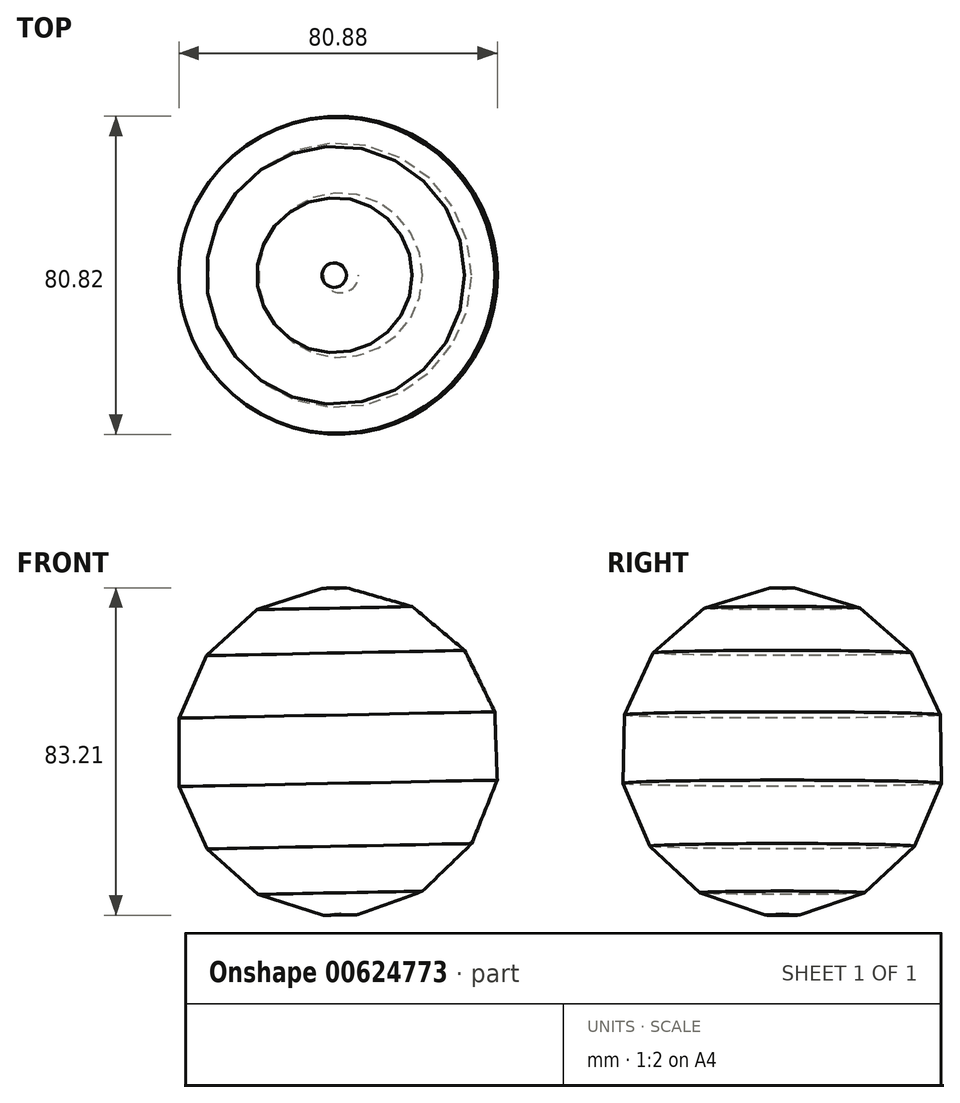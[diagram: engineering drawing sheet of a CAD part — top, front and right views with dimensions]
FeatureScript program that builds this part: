
annotation { "Feature Type Name" : "Feature", "Feature Type Description" : "" }
export const myFeature = defineFeature(function(context is Context, id is Id, definition is map)
    precondition{}
    {
        {
            var Q0;
            Q0=qCreatedBy(makeId("Front.planeOp"),FACE);
            var sketch = newSketch(context, id + "F0", { "sketchPlane" : qUnion([Q0])});
            skCircle(sketch, "E0.cCircle", {"center": v(-26.3, 29.34) * mm, "radius": 40.86 * mm, "construction": true});
            skLineSegment(sketch, "E0.0", {"start": v(8.37, 6.04) * mm, "end": v(-4.1, -6.04) * mm});
            skLineSegment(sketch, "E0.1", {"start": v(-4.1, -6.04) * mm, "end": v(-20.42, -12.01) * mm});
            skLineSegment(sketch, "E0.2", {"start": v(-20.42, -12.01) * mm, "end": v(-37.75, -10.83) * mm});
            skLineSegment(sketch, "E0.3", {"start": v(-37.75, -10.83) * mm, "end": v(-53.1, -2.7) * mm});
            skLineSegment(sketch, "E0.4", {"start": v(-53.1, -2.7) * mm, "end": v(-63.81, 10.97) * mm});
            skLineSegment(sketch, "E0.5", {"start": v(-63.81, 10.97) * mm, "end": v(-68.04, 27.82) * mm});
            skLineSegment(sketch, "E0.6", {"start": v(-68.04, 27.82) * mm, "end": v(-65.05, 44.93) * mm});
            skLineSegment(sketch, "E0.7", {"start": v(-65.05, 44.93) * mm, "end": v(-55.36, 59.34) * mm});
            skLineSegment(sketch, "E0.8", {"start": v(-55.36, 59.34) * mm, "end": v(-40.65, 68.57) * mm});
            skLineSegment(sketch, "E0.9", {"start": v(-40.65, 68.57) * mm, "end": v(-23.45, 71.02) * mm});
            skLineSegment(sketch, "E0.10", {"start": v(-23.45, 71.02) * mm, "end": v(-6.75, 66.26) * mm});
            skLineSegment(sketch, "E0.11", {"start": v(-6.75, 66.26) * mm, "end": v(6.58, 55.11) * mm});
            skLineSegment(sketch, "E0.12", {"start": v(6.58, 55.11) * mm, "end": v(14.22, 39.52) * mm});
            skLineSegment(sketch, "E0.13", {"start": v(14.22, 39.52) * mm, "end": v(14.85, 22.16) * mm});
            skLineSegment(sketch, "E0.14", {"start": v(14.85, 22.16) * mm, "end": v(8.37, 6.04) * mm});
            skPoint(sketch, "E0.0.midPoint", {"position": v(2.13, 0) * mm});
            skLineSegment(sketch, "E1", {"start": v(-26.7, 78.08) * mm, "end": v(-24.47, -32.39) * mm});
            skSolve(sketch);
        }
        {
            var Q0;
            Q0=makeQuery(id+"F0.imprint","IMPRINT",FACE,{"disambiguationData":[TD([[makeQuery(id+"F0.imprint","IMPRINT",EDGE,{"derivedFrom":sQuery(id+"F0.wireOp",EDGE,"E0.0")}),-1.0]])]});
            var Q1;
            Q1=sQuery(id+"F0.wireOp",EDGE,"E1");
            revolve(context, id + "F1", {"entities" : qUnion([Q0]), "axis" : qUnion([Q1]), "revolveType" : RevolveType.FULL});
        }
    });
